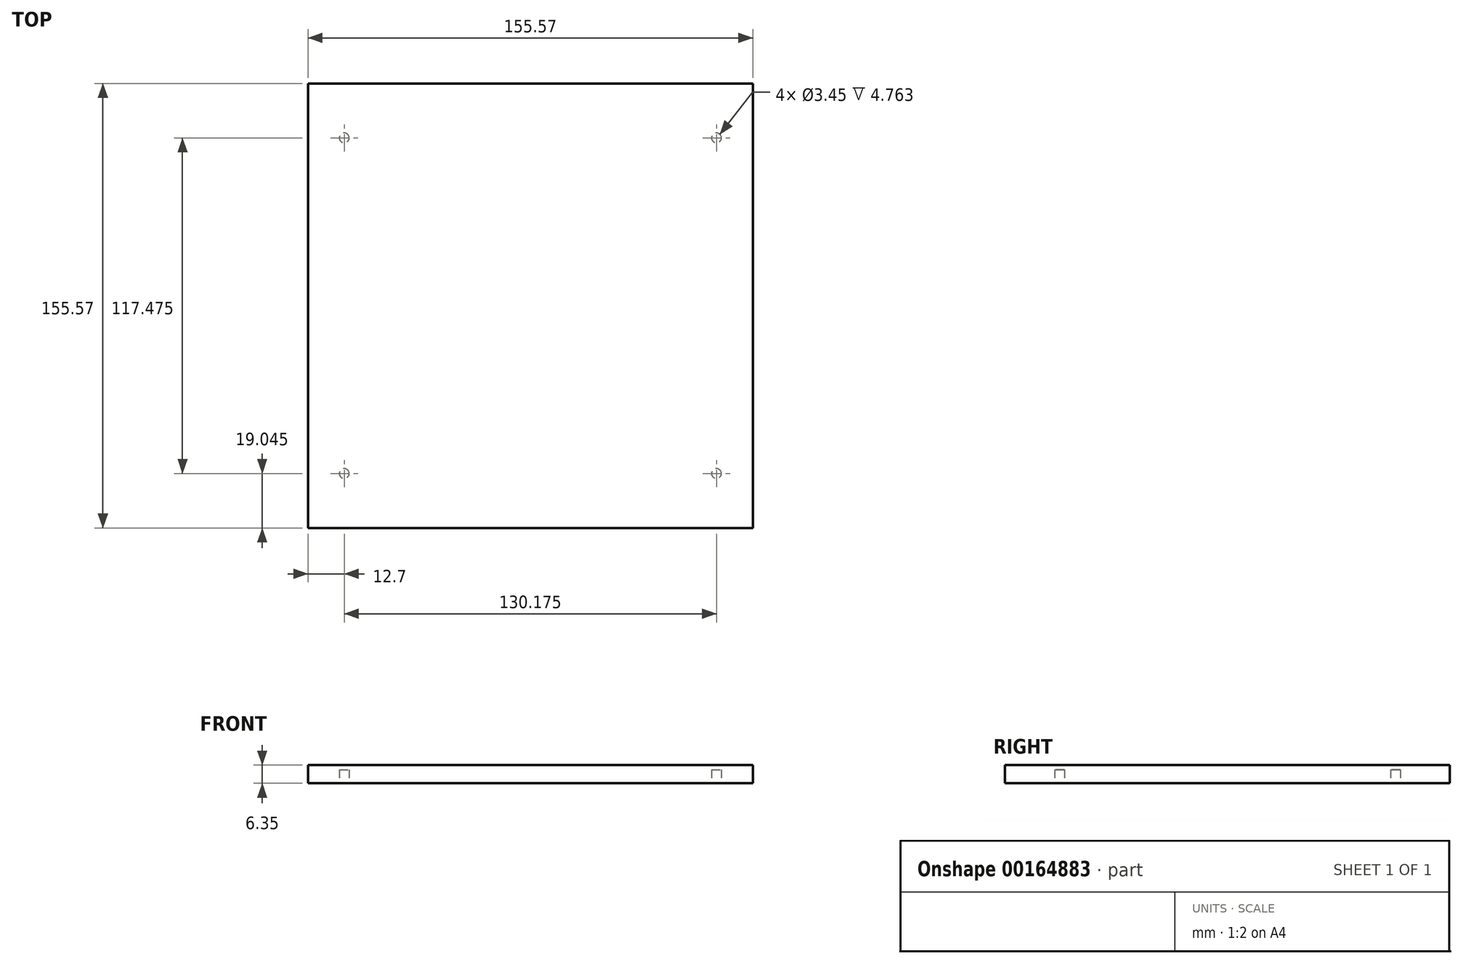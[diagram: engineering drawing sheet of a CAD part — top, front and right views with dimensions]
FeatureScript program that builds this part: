
annotation { "Feature Type Name" : "Feature", "Feature Type Description" : "" }
export const myFeature = defineFeature(function(context is Context, id is Id, definition is map)
    precondition{}
    {
        {
            var Q0;
            Q0=qCreatedBy(makeId("Top.planeOp"),FACE);
            var sketch = newSketch(context, id + "F0", { "sketchPlane" : qUnion([Q0])});
            skLineSegment(sketch, "E0.bottom", {"start": v(0, 0) * mm, "end": v(155.58, 0) * mm});
            skLineSegment(sketch, "E0.top", {"start": v(0, -155.58) * mm, "end": v(155.58, -155.58) * mm});
            skLineSegment(sketch, "E0.left", {"start": v(0, 0) * mm, "end": v(0, -155.58) * mm});
            skLineSegment(sketch, "E0.right", {"start": v(155.58, 0) * mm, "end": v(155.58, -155.58) * mm});
            skSolve(sketch);
        }
        {
            var Q0;
            Q0=qSketchRegion(id+"F0",true);
            extrude(context, id + "F1", {"entities" : qUnion([Q0]), "depth" : 6.35 * mm});
        }
        {
            var Q0;
            Q0=makeQuery(id+"F1.opExtrude","CAP_FACE",FACE,{"disambiguationData":[OSD([sQuery(id+"F0.wireOp",EDGE,"E0.bottom"),sQuery(id+"F0.wireOp",EDGE,"E0.top"),sQuery(id+"F0.wireOp",EDGE,"E0.left"),sQuery(id+"F0.wireOp",EDGE,"E0.right")])],"isStart":true});
            var sketch = newSketch(context, id + "F2", { "sketchPlane" : qUnion([Q0])});
            skLineSegment(sketch, "E1", {"start": v(77.79, 155.58) * mm, "end": v(77.79, 0) * mm, "construction": true});
            skLineSegment(sketch, "E2.bottom", {"start": v(142.88, 136.53) * mm, "end": v(12.7, 136.53) * mm, "construction": true});
            skLineSegment(sketch, "E2.top", {"start": v(142.88, 19.05) * mm, "end": v(12.7, 19.05) * mm, "construction": true});
            skLineSegment(sketch, "E2.left", {"start": v(142.88, 136.53) * mm, "end": v(142.88, 19.05) * mm, "construction": true});
            skLineSegment(sketch, "E2.right", {"start": v(12.7, 136.53) * mm, "end": v(12.7, 19.05) * mm, "construction": true});
            skPoint(sketch, "E2.middle", {"position": v(77.79, 77.79) * mm});
            skLineSegment(sketch, "E3.bottom", {"start": v(142.88, 136.53) * mm, "end": v(155.58, 136.53) * mm, "construction": true});
            skLineSegment(sketch, "E3.top", {"start": v(142.88, 155.58) * mm, "end": v(155.58, 155.58) * mm, "construction": true});
            skLineSegment(sketch, "E3.left", {"start": v(142.88, 136.53) * mm, "end": v(142.88, 155.58) * mm, "construction": true});
            skLineSegment(sketch, "E3.right", {"start": v(155.58, 136.53) * mm, "end": v(155.58, 155.58) * mm, "construction": true});
            skCircle(sketch, "E4", {"center": v(142.88, 136.53) * mm, "radius": 1.73 * mm});
            skCircle(sketch, "E5", {"center": v(142.88, 19.05) * mm, "radius": 1.73 * mm});
            skCircle(sketch, "E6", {"center": v(12.7, 19.05) * mm, "radius": 1.73 * mm});
            skCircle(sketch, "E7", {"center": v(12.7, 136.53) * mm, "radius": 1.73 * mm});
            skSolve(sketch);
        }
        {
            var Q0;
            Q0=qSketchRegion(id+"F2",true);
            extrude(context, id + "F3", {"entities" : qUnion([Q0]), "operationType" : NewBodyOperationType.REMOVE, "oppositeDirection" : true, "depth" : 4.76 * mm});
        }
    });
